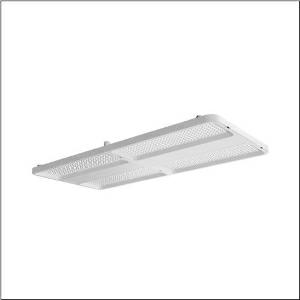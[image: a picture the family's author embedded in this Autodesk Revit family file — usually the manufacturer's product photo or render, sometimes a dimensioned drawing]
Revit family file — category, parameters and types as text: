
# Revit family: highbay_21_maxi_52hn12db4rda
name_source: partatom
category: Lighting Fixtures
units: mm (PartAtom-declared; Revit-internal decimal feet)

## family parameters
Cut with Voids When Loaded = No
Host = Face
Light Source = No
Part Type = Normal
Room Calculation Point = No
Round Connector Dimension = Use Diameter
Shared = No

## types (1)
- --- (1 x LED, 7000 lm, 38.3 W, 4000K)
    Apparent Load = 38 VA
    CIE Flux Codes = 90 98 100 100 100
    Color Rendering = 80
    Color Temperature = 4000K
    Default Elevation = 1800 mm
    Description = high bay luminaire Highbay 21 maxi; direct symmetric wide distribution, light control with lens of PMMA; UGR ≤ 22 (X = 4H | Y = 8H | S = 0.25H | reflection values 70/50/20); luminous flux: 45.000lm; light colour: 840, colour temperature: 4000K, MacAdam ≤ 3 SDCM (initial), colour rendering: CRI > 80; luminous efficacy: 188lm/W; rated service life: 75.000h (L80/B50) at AT= ta max; control: DALI 2; housing frame of high-performance plastic PA6, matt traffic white (RAL 9016); cover of PMMA; dimension (LxWxH): 946 x 442 x 72mm; luminaire connection: terminal, 5-pole, max. 2.5mm² (cable entry for one cable, Ø 8.5..16mm); mains connection: 230..240V, AC/DC 0/50..60Hz; connected load: 239,3W; protection rating (complete): IP66; insulation class (complete): insulation class I (protective earthing); protection symbol: D; impact resistance: IK08; halogen-free wiring; for central battery installations according to DIN EN 60598-2-22; LABS conformity tested according to VDMA 24364:2018-05; corresponds to IFS (International Featured Standards) requirements for safety and quality in the food industry; certification: CE, ENEC, VDE, UKCA; permissible operating ambient temperature: -40..+55°C (reducing of maximum allowable ambient temperature of 5°C with ceiling mounting); packaging unit: 1 piece; (delivery without accessories; please order mounting accessories separately)
    Height = 72 mm  [stored 0.23622 ft]
    Lamp = 1 x LED
    Lamp Light Flux = 7000 lm
    Lamp Power = 38.3 W
    Lamp count = 1
    Length = 946 mm
    Luminous efficacy = 183 lm/W
    Manufacturer = Siteco
    ModVariant = No
    Model = 52HN12DB4RDA
    Mounting Place = Ceiling
    Mounting Type = Pendant
    Number of Poles = 1
    OnlyDefault = Yes
    Power Factor = 1
    Product Name = Highbay 21 maxi
    Product group = high bay luminaire
    ProductGroupID = 901
    Protection Class = Protection class I
    Protection Degree = IP 66
    RLX_Detail_Level = 1
    RLX_Emergency_Light_Flux = 0 lm
    RLX_Emergency_Type = 0
    RLX_Emergency_Type_DB = No
    RlxData = <blob elided: 23125 chars, md5=2c4cde7c>
    Socket = socket
    Standby Power = 0 W
    System Light Flux = 7000 lm
    System Power = 38 W
    Type Comments = : DC mode (central or group accumulator) initial emergency light level
    Type Image = l_1363244.jpg
    URL = http://relux.com
    VarID = @adj_000559
    Voltage = 0 V
    Weight = 0.00 kg
    Width = 442 mm

note: [stored X ft] marks values corroborated as IEEE doubles in the binary element streams (Revit-internal decimal feet)

## geometry (parser evidence)
native form markers: Blend x4, Sweep x11
no freeform markers — native parametric forms only
